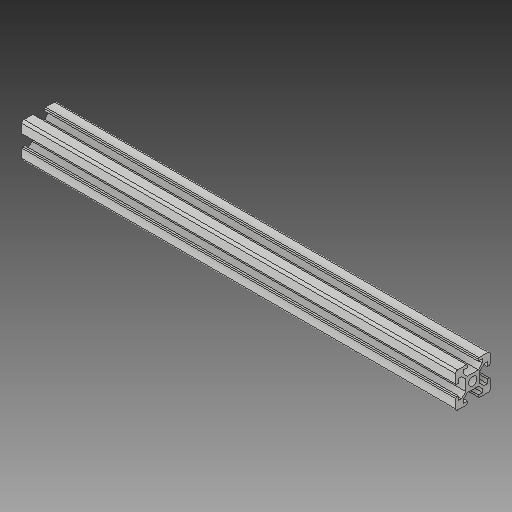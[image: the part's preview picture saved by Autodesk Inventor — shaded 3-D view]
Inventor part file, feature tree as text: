
AUTODESK INVENTOR PART (.ipt)
format: ipt  version: 2019 (Build 230136000, 136)  size: 173,568 bytes
history: native  units: in
note: dims shown in document units (in); Inventor stores cm internally (conversion verified against a paired STEP export)
features: extrude x1, fillet x1, sketch x1
ambient origin geometry x8: Origin, YZ Plane, XZ Plane, XY Plane, X Axis, Y Axis, Z Axis, Center Point
bodies: Solid1 (feature_tree)
feature tree (3):
  extrude  "Extrusion1"  Depth=0.0492in
  fillet  "Fillet1"  [1 undecoded]
  sketch  "Sketch1"  dims[d0=0.1969in d3=0.1417in d4=45.0deg d5=0.122in d7=0.2165in d8=0.063in d11=0.1693in d12=9.8425in d13=0.0in d14=0.0492in]
note: 1 required parameter value undecoded (feature->parameter linkage not recoverable at this tier; creation-order binding heuristic only, values carry confidence <= 0.55)
